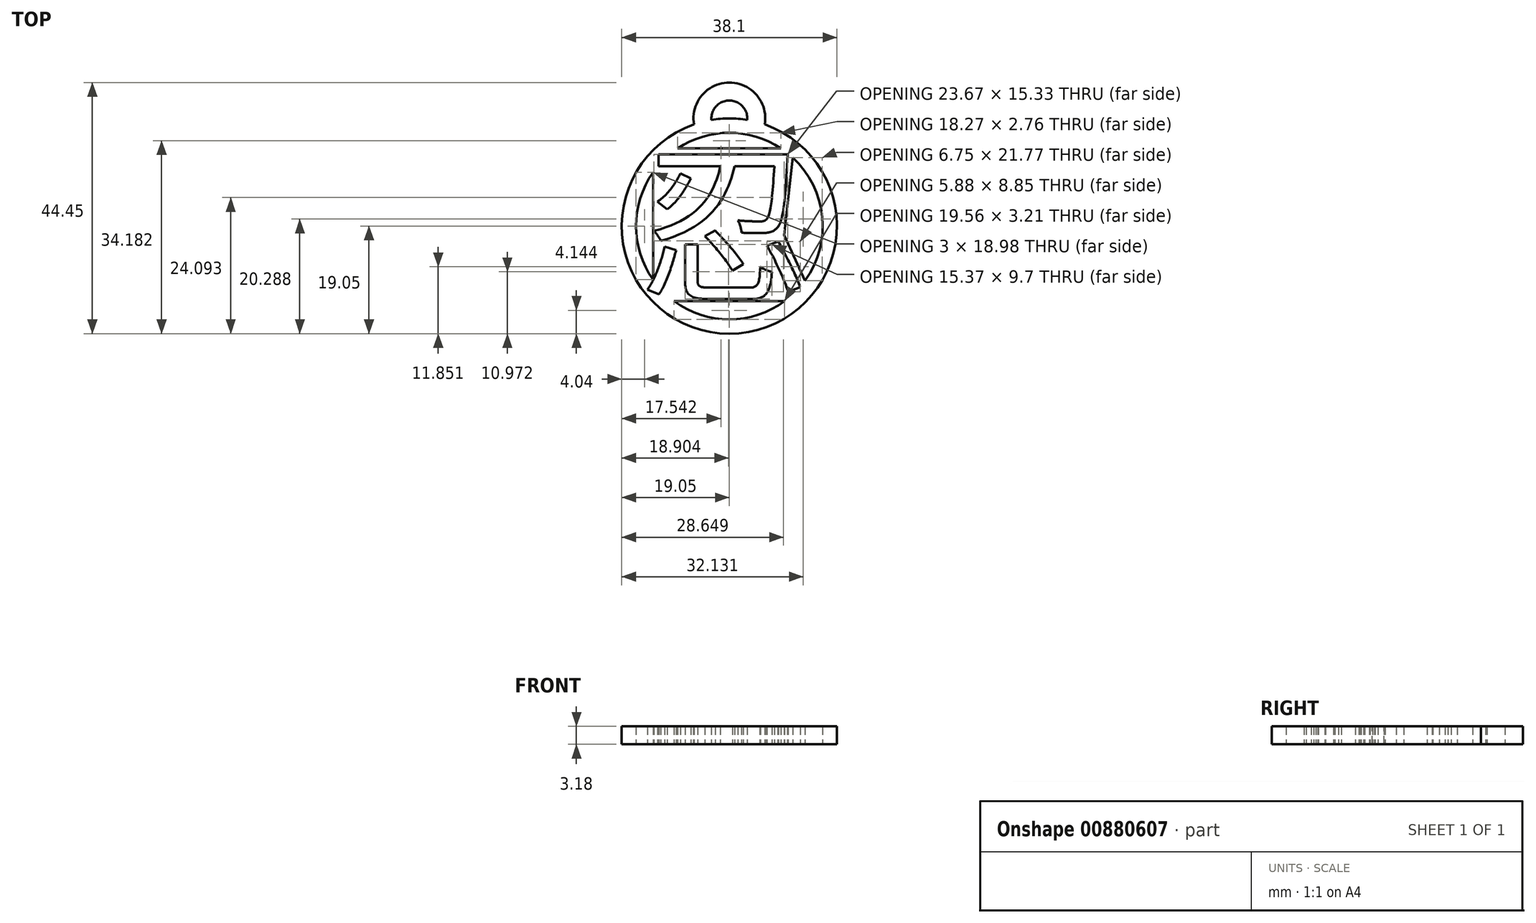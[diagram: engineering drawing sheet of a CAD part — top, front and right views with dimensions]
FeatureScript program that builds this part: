
annotation { "Feature Type Name" : "Feature", "Feature Type Description" : "" }
export const myFeature = defineFeature(function(context is Context, id is Id, definition is map)
    precondition{}
    {
        {
            var Q0;
            Q0=qCreatedBy(makeId("Top.planeOp"),FACE);
            var sketch = newSketch(context, id + "F0", { "sketchPlane" : qUnion([Q0])});
            skArc(sketch, "E0", {"start": v(-6.26, 18) * mm, "mid": v(0, -19.05) * mm, "end": v(6.26, 18) * mm});
            skArc(sketch, "E1", {"start": v(6.26, 18) * mm, "mid": v(0, 25.4) * mm, "end": v(-6.26, 18) * mm});
            skArc(sketch, "E2", {"start": v(3.16, 18.79) * mm, "mid": v(0, 22.23) * mm, "end": v(-3.16, 18.79) * mm});
            skArc(sketch, "E3.trimOffspring", {"start": v(3.16, 18.79) * mm, "mid": v(0, 19.05) * mm, "end": v(-3.16, 18.79) * mm});
            skText(sketch, "E4", { "text": "忍", "fontName": "NotoSansCJKsc-Regular.otf"});
            skCircle(sketch, "E5", {"center": v(0, 0) * mm, "radius": 16.51 * mm});
            skLineSegment(sketch, "E6", {"start": v(-9.13, 13.75) * mm, "end": v(9.13, 13.75) * mm});
            skLineSegment(sketch, "E7", {"start": v(-9.78, -13.3) * mm, "end": v(9.78, -13.3) * mm});
            skLineSegment(sketch, "E8", {"start": v(9.7, -1.63) * mm, "end": v(11.2, 12.12) * mm});
            skLineSegment(sketch, "E9", {"start": v(-13.5, -9.5) * mm, "end": v(-13.5, 9.5) * mm});
            skLineSegment(sketch, "E10", {"start": v(9.7, -1.63) * mm, "end": v(13.4, -9.65) * mm});
            const initialGuessF0  = {"E4": [-0.01604, -0.01108, 1, 0, 0.02182]};
            skSetInitialGuess(sketch, initialGuessF0);
            skSolve(sketch);
        }
        {
            var Q0;
            Q0 = qSketchRegion(id + "F0", true);
            var Q1;
            Q1=makeQuery(id+"F0.imprint","IMPRINT",FACE,{"disambiguationData":[TD([[makeQuery(id+"F0.imprint","IMPRINT",EDGE,{"derivedFrom":sQuery(id+"F0.wireOp",EDGE,"E4.sketch_text.stroke-0")}),-1.0]])]});
            var Q2;
            {var subQ0=sQuery(id+"F0.wireOp",EDGE,"E5");var subQ1=sQuery(id+"F0.wireOp",EDGE,"E4.sketch_text.stroke-8");var subQ2=makeQuery(id+"F0.imprint","INTERSECT",VERTEX,{"disambiguationData":[OD(0.0)],"derivedFrom":[subQ1,subQ0]});Q2=makeQuery(id+"F0.imprint","IMPRINT",FACE,{"disambiguationData":[TD([[makeQuery(id+"F0.imprint","IMPRINT",EDGE,{"disambiguationData":[TD([[subQ2,-1.0]])],"derivedFrom":subQ1}),-1.0]])]});}
            extrude(context, id + "F1", {"entities" : qUnion([Q0, Q1, Q2]), "depth" : 3.17 * mm, "offsetDistance" : 25.4 * mm});
        }
    });
